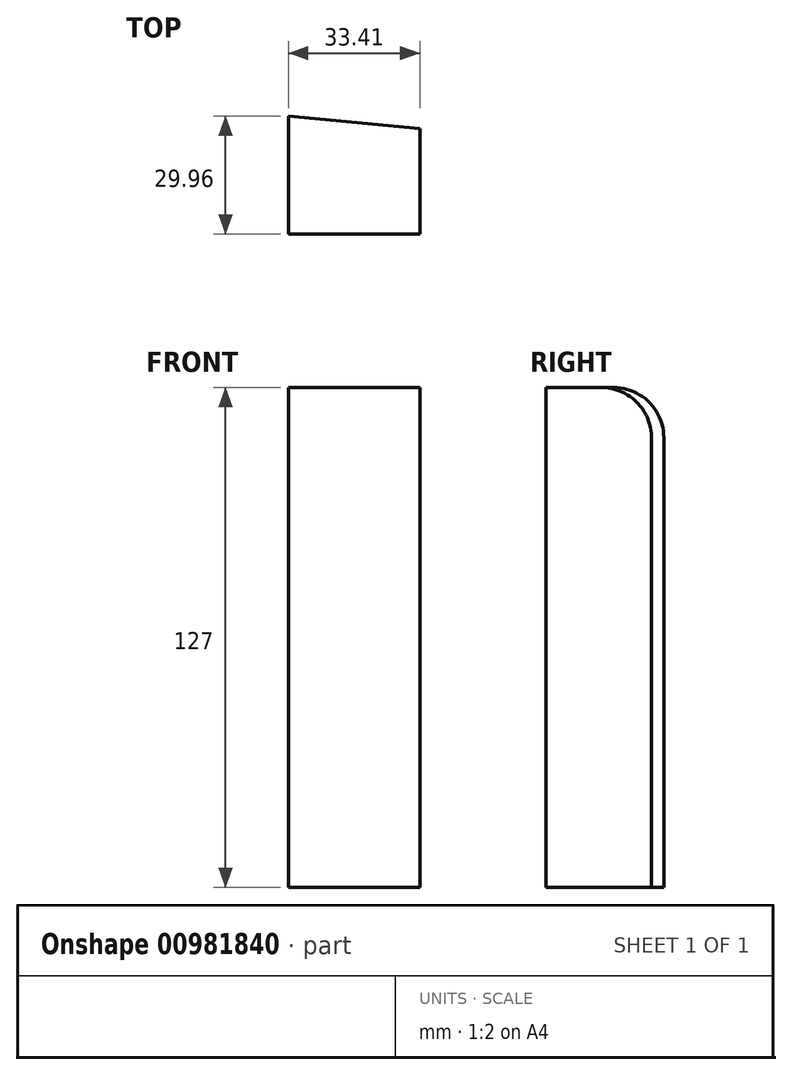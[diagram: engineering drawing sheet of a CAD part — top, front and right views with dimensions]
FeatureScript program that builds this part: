
annotation { "Feature Type Name" : "Feature", "Feature Type Description" : "" }
export const myFeature = defineFeature(function(context is Context, id is Id, definition is map)
    precondition{}
    {
        {
            var Q0;
            Q0=qCreatedBy(makeId("Top.planeOp"),FACE);
            var sketch = newSketch(context, id + "F0", { "sketchPlane" : qUnion([Q0])});
            skLineSegment(sketch, "E0", {"start": v(-23.03, 61.04) * mm, "end": v(-23.03, 34.23) * mm});
            skLineSegment(sketch, "E1", {"start": v(-23.03, 34.23) * mm, "end": v(-56.44, 34.23) * mm});
            skLineSegment(sketch, "E2", {"start": v(-56.44, 34.23) * mm, "end": v(-56.44, 64.19) * mm});
            skLineSegment(sketch, "E3", {"start": v(-56.44, 64.19) * mm, "end": v(-23.03, 61.04) * mm});
            skSolve(sketch);
        }
        {
            var Q0;
            Q0=makeQuery(id+"F0.imprint","IMPRINT",FACE,{"disambiguationData":[TD([[makeQuery(id+"F0.imprint","IMPRINT",EDGE,{"derivedFrom":sQuery(id+"F0.wireOp",EDGE,"E0")}),-1.0]])]});
            extrude(context, id + "F1", {"entities" : qUnion([Q0]), "depth" : 127 * mm, "offsetDistance" : 25.4 * mm});
        }
        {
            var Q0;
            Q0=makeQuery(id+"F1.opExtrude","CAP_EDGE",EDGE,{"disambiguationData":[OSD([sQuery(id+"F0.wireOp",EDGE,"E3")])],"isStart":false});
            fillet(context, id + "F2", {"entities" : qUnion([Q0]), "radius" : 12.7 * mm, "tangentPropagation" : true, "allowEdgeOverflow" : false});
        }
    });
